FCSTD DOCUMENT  (FreeCAD 0.20R29603 (Git))
Label: CNC_Cut_Layer_Designs
License: All rights reserved
LicenseURL: http://en.wikipedia.org/wiki/All_rights_reserved
objects: Sketcher::SketchObject×10, PartDesign::Body×3
note: 13 computed .brp shape members not serialized (recipe doc carries the construction recipe); baked Part::Feature solids carry a one-line shape summary decoded from their .brp

FEATURE [Sketcher::SketchObject] Sketch007  label="Bottom"
  AttachmentOffset = pos=(496,62,0) rot=(0,0,1;0rad)
  FullyConstrained = true
  MapMode = 5
  Placement = pos=(496,62,0) rot=(0,0,1;0rad)
  Support = -> [XY_Plane004]
  sketch-geometry (20):
    g0: LineSegment StartX=-168 StartY=203 StartZ=0 EndX=168 EndY=203 EndZ=0
    g1: LineSegment StartX=168 StartY=203 StartZ=0 EndX=168 EndY=-203 EndZ=0
    g2: LineSegment StartX=168 StartY=-203 StartZ=0 EndX=-168 EndY=-203 EndZ=0
    g3: LineSegment StartX=-168 StartY=-203 StartZ=0 EndX=-168 EndY=203 EndZ=0
    g4: LineSegment StartX=-155 StartY=190 StartZ=0 EndX=155 EndY=190 EndZ=0
    g5: LineSegment StartX=155 StartY=190 StartZ=0 EndX=155 EndY=-190 EndZ=0
    g6: LineSegment StartX=155 StartY=-190 StartZ=0 EndX=-155 EndY=-190 EndZ=0
    g7: LineSegment StartX=-155 StartY=-190 StartZ=0 EndX=-155 EndY=190 EndZ=0
    g8: LineSegment StartX=155 StartY=190 StartZ=0 EndX=168 EndY=203 EndZ=0
    g9: LineSegment StartX=-168 StartY=-203 StartZ=0 EndX=-155 EndY=-190 EndZ=0
    g10: Circle CenterX=-95 CenterY=190 CenterZ=0 NormalX=0 NormalY=0 NormalZ=1 AngleXU=0 Radius=3.1
    g11: Circle CenterX=95 CenterY=190 CenterZ=0 NormalX=0 NormalY=0 NormalZ=1 AngleXU=0 Radius=3.1
    g12: Circle CenterX=155 CenterY=130 CenterZ=0 NormalX=0 NormalY=0 NormalZ=1 AngleXU=0 Radius=3.1
    g13: Circle CenterX=155 CenterY=-130 CenterZ=0 NormalX=0 NormalY=0 NormalZ=1 AngleXU=0 Radius=3.1
    g14: Circle CenterX=95 CenterY=-190 CenterZ=0 NormalX=0 NormalY=0 NormalZ=1 AngleXU=0 Radius=3.1
    g15: Circle CenterX=-95 CenterY=-190 CenterZ=0 NormalX=0 NormalY=0 NormalZ=1 AngleXU=0 Radius=3.1
    g16: Circle CenterX=-155 CenterY=-130 CenterZ=0 NormalX=0 NormalY=0 NormalZ=1 AngleXU=0 Radius=3.1
    g17: Circle CenterX=-155 CenterY=130 CenterZ=0 NormalX=0 NormalY=0 NormalZ=1 AngleXU=0 Radius=3.1
    g18: Circle CenterX=-155 CenterY=0 CenterZ=0 NormalX=0 NormalY=0 NormalZ=1 AngleXU=0 Radius=3.1
    g19: Circle CenterX=155 CenterY=0 CenterZ=0 NormalX=0 NormalY=0 NormalZ=1 AngleXU=0 Radius=3.1
  constraints (49):
    c: Coincident(g0,g1)
    c: Coincident(g1,g2)
    c: Coincident(g2,g3)
    c: Coincident(g3,g0)
    c: Horizontal(g2)
    c: Vertical(g1)
    c: DistanceX(g0,g0) = 336
    c: DistanceY(g3,g3) = 406
    c: Symmetric(g0,g0,g-2)
    c: Symmetric(g0,g2,g-1)
    c: Coincident(g4,g5)
    c: Coincident(g5,g6)
    c: Coincident(g6,g7)
    c: Coincident(g7,g4)
    c: Horizontal(g4)
    c: Horizontal(g6)
    c: Vertical(g5)
    c: Vertical(g7)
    c: Coincident(g8,g4)
    c: Coincident(g8,g0)
    c: Angle(g8) = 0.785398
    c: DistanceY(g4,g0) = 13
    c: Coincident(g9,g2)
    c: Coincident(g9,g6)
    c: Angle(g9) = 0.785398
    c: DistanceX(g2,g6) = 13
    c: PointOnObject(g10,g4)
    c: PointOnObject(g12,g5)
    c: PointOnObject(g14,g6)
    c: PointOnObject(g16,g7)
    c: Diameter(g17) = 6.2
    c: Equal(g17, g10-g13) x4
    c: Equal(g17,g16)
    c: Equal(g17,g15)
    c: Equal(g17,g14)
    c: Symmetric(g17,g16,g-1)
    c: Symmetric(g12,g13,g-1)
    c: DistanceY(g12,g17) = 0
    c: Symmetric(g15,g14,g-2)
    c: Symmetric(g10,g11,g-2)
    c: DistanceX(g10,g15) = 0
    c: DistanceX(g14,g5) = 60
    c: DistanceY(g12,g4) = 60
    c: PointOnObject(g18,g-1)
    c: PointOnObject(g19,g-1)
    c: Diameter(g19) = 6.2
    c: Equal(g19,g18)
    c: PointOnObject(g18,g7)
    c: PointOnObject(g19,g5)
FEATURE [Sketcher::SketchObject] Sketch008  label="Top"
  AttachmentOffset = pos=(496,473,0) rot=(0,0,1;0rad)
  FullyConstrained = true
  MapMode = 5
  Placement = pos=(496,473,0) rot=(0,0,1;0rad)
  Support = -> [XY_Plane004]
  sketch-geometry (18):
    g0: LineSegment StartX=-168 StartY=203 StartZ=0 EndX=168 EndY=203 EndZ=0
    g1: LineSegment StartX=168 StartY=203 StartZ=0 EndX=168 EndY=-203 EndZ=0
    g2: LineSegment StartX=168 StartY=-203 StartZ=0 EndX=-168 EndY=-203 EndZ=0
    g3: LineSegment StartX=-168 StartY=-203 StartZ=0 EndX=-168 EndY=203 EndZ=0
    g4: LineSegment StartX=-155 StartY=190 StartZ=0 EndX=155 EndY=190 EndZ=0
    g5: LineSegment StartX=155 StartY=190 StartZ=0 EndX=155 EndY=-190 EndZ=0
    g6: LineSegment StartX=155 StartY=-190 StartZ=0 EndX=-155 EndY=-190 EndZ=0
    g7: LineSegment StartX=-155 StartY=-190 StartZ=0 EndX=-155 EndY=190 EndZ=0
    g8: LineSegment StartX=155 StartY=190 StartZ=0 EndX=168 EndY=203 EndZ=0
    g9: LineSegment StartX=-168 StartY=-203 StartZ=0 EndX=-155 EndY=-190 EndZ=0
    g10: Circle CenterX=-95 CenterY=190 CenterZ=0 NormalX=0 NormalY=0 NormalZ=1 AngleXU=0 Radius=3.1
    g11: Circle CenterX=95 CenterY=190 CenterZ=0 NormalX=0 NormalY=0 NormalZ=1 AngleXU=0 Radius=3.1
    g12: Circle CenterX=155 CenterY=100 CenterZ=0 NormalX=0 NormalY=0 NormalZ=1 AngleXU=0 Radius=3.1
    g13: Circle CenterX=155 CenterY=-100 CenterZ=0 NormalX=0 NormalY=0 NormalZ=1 AngleXU=0 Radius=3.1
    g14: Circle CenterX=95 CenterY=-190 CenterZ=0 NormalX=0 NormalY=0 NormalZ=1 AngleXU=0 Radius=3.1
    g15: Circle CenterX=-95 CenterY=-190 CenterZ=0 NormalX=0 NormalY=0 NormalZ=1 AngleXU=0 Radius=3.1
    g16: Circle CenterX=-155 CenterY=-100 CenterZ=0 NormalX=0 NormalY=0 NormalZ=1 AngleXU=0 Radius=3.1
    g17: Circle CenterX=-155 CenterY=100 CenterZ=0 NormalX=0 NormalY=0 NormalZ=1 AngleXU=0 Radius=3.1
  constraints (43):
    c: Coincident(g0,g1)
    c: Coincident(g1,g2)
    c: Coincident(g2,g3)
    c: Coincident(g3,g0)
    c: Horizontal(g2)
    c: Vertical(g1)
    c: DistanceX(g0,g0) = 336
    c: DistanceY(g3,g3) = 406
    c: Symmetric(g0,g0,g-2)
    c: Symmetric(g0,g2,g-1)
    c: Coincident(g4,g5)
    c: Coincident(g5,g6)
    c: Coincident(g6,g7)
    c: Coincident(g7,g4)
    c: Horizontal(g4)
    c: Horizontal(g6)
    c: Vertical(g5)
    c: Vertical(g7)
    c: Coincident(g8,g4)
    c: Coincident(g8,g0)
    c: Angle(g8) = 0.785398
    c: DistanceY(g4,g0) = 13
    c: Coincident(g9,g2)
    c: Coincident(g9,g6)
    c: Angle(g9) = 0.785398
    c: DistanceX(g2,g6) = 13
    c: PointOnObject(g10,g4)
    c: PointOnObject(g12,g5)
    c: PointOnObject(g14,g6)
    c: PointOnObject(g16,g7)
    c: Diameter(g17) = 6.2
    c: Equal(g17, g10-g13) x4
    c: Equal(g17,g16)
    c: Equal(g17,g15)
    c: Equal(g17,g14)
    c: Symmetric(g17,g16,g-1)
    c: Symmetric(g12,g13,g-1)
    c: DistanceY(g12,g17) = 0
    c: Symmetric(g15,g14,g-2)
    c: Symmetric(g10,g11,g-2)
    c: DistanceX(g10,g15) = 0
    c: DistanceX(g14,g5) = 60
    c: DistanceY(g12,g4) = 90
FEATURE [Sketcher::SketchObject] Sketch009  label="Left"
  AttachmentOffset = pos=(60,62,0) rot=(0,0,1;1.5708rad)
  FullyConstrained = true
  MapMode = 5
  Placement = pos=(60,62,0) rot=(0,0,1;1.5708rad)
  Support = -> [XY_Plane004]
  sketch-geometry (24):
    g0: LineSegment StartX=-203 StartY=263 StartZ=0 EndX=203 EndY=263 EndZ=0
    g1: LineSegment StartX=203 StartY=263 StartZ=0 EndX=203 EndY=-263 EndZ=0
    g2: LineSegment StartX=203 StartY=-263 StartZ=0 EndX=-203 EndY=-263 EndZ=0
    g3: LineSegment StartX=-203 StartY=-263 StartZ=0 EndX=-203 EndY=263 EndZ=0
    g4: LineSegment StartX=-190 StartY=250 StartZ=0 EndX=190 EndY=250 EndZ=0
    g5: LineSegment StartX=190 StartY=250 StartZ=0 EndX=190 EndY=-250 EndZ=0
    g6: LineSegment StartX=190 StartY=-250 StartZ=0 EndX=-190 EndY=-250 EndZ=0
    g7: LineSegment StartX=-190 StartY=-250 StartZ=0 EndX=-190 EndY=250 EndZ=0
    g8: LineSegment StartX=190 StartY=250 StartZ=0 EndX=203 EndY=263 EndZ=0
    g9: LineSegment StartX=190 StartY=-250 StartZ=0 EndX=203 EndY=-263 EndZ=0
    g10: LineSegment StartX=-203 StartY=263 StartZ=0 EndX=-173 EndY=263 EndZ=0
    g11: LineSegment StartX=-173 StartY=263 StartZ=0 EndX=-173 EndY=233 EndZ=0
    g12: LineSegment StartX=-173 StartY=233 StartZ=0 EndX=-203 EndY=233 EndZ=0
    g13: LineSegment StartX=-203 StartY=233 StartZ=0 EndX=-203 EndY=263 EndZ=0
    g14: Circle CenterX=-190 CenterY=175 CenterZ=0 NormalX=0 NormalY=0 NormalZ=1 AngleXU=0 Radius=3.1
    g15: Circle CenterX=-100 CenterY=250 CenterZ=0 NormalX=0 NormalY=0 NormalZ=1 AngleXU=0 Radius=3.1
    g16: Circle CenterX=100 CenterY=250 CenterZ=0 NormalX=0 NormalY=0 NormalZ=1 AngleXU=0 Radius=3.1
    g17: Circle CenterX=190 CenterY=175 CenterZ=0 NormalX=0 NormalY=0 NormalZ=1 AngleXU=0 Radius=3.1
    g18: Circle CenterX=-190 CenterY=0 CenterZ=0 NormalX=0 NormalY=0 NormalZ=1 AngleXU=0 Radius=3.1
    g19: Circle CenterX=-190 CenterY=-175 CenterZ=0 NormalX=0 NormalY=0 NormalZ=1 AngleXU=0 Radius=3.1
    g20: Circle CenterX=-100 CenterY=-250 CenterZ=0 NormalX=0 NormalY=0 NormalZ=1 AngleXU=0 Radius=3.1
    g21: Circle CenterX=100 CenterY=-250 CenterZ=0 NormalX=0 NormalY=0 NormalZ=1 AngleXU=0 Radius=3.1
    g22: Circle CenterX=190 CenterY=-175 CenterZ=0 NormalX=0 NormalY=0 NormalZ=1 AngleXU=0 Radius=3.1
    g23: Circle CenterX=190 CenterY=0 CenterZ=0 NormalX=0 NormalY=0 NormalZ=1 AngleXU=0 Radius=3.1
  constraints (62):
    c: Coincident(g0,g1)
    c: Coincident(g1,g2)
    c: Coincident(g2,g3)
    c: Coincident(g3,g0)
    c: Horizontal(g2)
    c: Vertical(g1)
    c: Symmetric(g0,g0,g-2)
    c: Symmetric(g0,g2,g-1)
    c: DistanceX(g0,g0) = 406
    c: DistanceY(g1,g0) = 526
    c: Coincident(g4,g5)
    c: Coincident(g5,g6)
    c: Coincident(g6,g7)
    c: Coincident(g7,g4)
    c: Horizontal(g6)
    c: Vertical(g5)
    c: Vertical(g7)
    c: Coincident(g8,g4)
    c: Coincident(g8,g0)
    c: Angle(g8) = 0.785398
    c: DistanceX(g4,g0) = 13
    c: Symmetric(g4,g4,g-2)
    c: Coincident(g9,g5)
    c: Coincident(g9,g1)
    c: Angle(g9) = -0.785398
    c: Coincident(g10,g11)
    c: Coincident(g11,g12)
    c: Coincident(g12,g13)
    c: Coincident(g13,g10)
    c: Horizontal(g10)
    c: Horizontal(g12)
    c: Vertical(g11)
    c: Vertical(g13)
    c: Coincident(g10,g0)
    c: Equal(g12,g11)
    c: DistanceY(g11,g11) = 30
    c: PointOnObject(g14,g7)
    c: PointOnObject(g15,g4)
    c: PointOnObject(g17,g5)
    c: PointOnObject(g18,g-1)
    c: PointOnObject(g20,g6)
    c: PointOnObject(g23,g-1)
    c: PointOnObject(g23,g5)
    c: PointOnObject(g18,g7)
    c: Symmetric(g14,g19,g-1)
    c: Symmetric(g15,g16,g-2)
    c: Symmetric(g17,g22,g-1)
    c: DistanceY(g17,g14) = 0
    c: Symmetric(g20,g21,g-2)
    c: DistanceX(g21,g16) = 0
    c: Equal(g20,g21)
    c: Equal(g20,g22)
    c: Equal(g20,g23)
    c: Equal(g20,g17)
    c: Equal(g20,g16)
    c: Equal(g20,g15)
    c: Equal(g20,g14)
    c: Equal(g20,g18)
    c: Equal(g20,g19)
    c: Diameter(g20) = 6.2
    c: DistanceX(g16,g4) = 90
    c: DistanceY(g14,g4) = 75
FEATURE [Sketcher::SketchObject] Sketch010  label="Right"
  AttachmentOffset = pos=(60,473,0) rot=(0,0,1;1.5708rad)
  FullyConstrained = true
  MapMode = 5
  Placement = pos=(60,473,0) rot=(0,0,1;1.5708rad)
  Support = -> [XY_Plane004]
  sketch-geometry (24):
    g0: LineSegment StartX=-203 StartY=263 StartZ=0 EndX=203 EndY=263 EndZ=0
    g1: LineSegment StartX=203 StartY=263 StartZ=0 EndX=203 EndY=-263 EndZ=0
    g2: LineSegment StartX=203 StartY=-263 StartZ=0 EndX=-203 EndY=-263 EndZ=0
    g3: LineSegment StartX=-203 StartY=-263 StartZ=0 EndX=-203 EndY=263 EndZ=0
    g4: LineSegment StartX=-190 StartY=250 StartZ=0 EndX=190 EndY=250 EndZ=0
    g5: LineSegment StartX=190 StartY=250 StartZ=0 EndX=190 EndY=-250 EndZ=0
    g6: LineSegment StartX=190 StartY=-250 StartZ=0 EndX=-190 EndY=-250 EndZ=0
    g7: LineSegment StartX=-190 StartY=-250 StartZ=0 EndX=-190 EndY=250 EndZ=0
    g8: LineSegment StartX=190 StartY=250 StartZ=0 EndX=203 EndY=263 EndZ=0
    g9: LineSegment StartX=190 StartY=-250 StartZ=0 EndX=203 EndY=-263 EndZ=0
    g10: LineSegment StartX=-203 StartY=263 StartZ=0 EndX=-173 EndY=263 EndZ=0
    g11: LineSegment StartX=-173 StartY=263 StartZ=0 EndX=-173 EndY=233 EndZ=0
    g12: LineSegment StartX=-173 StartY=233 StartZ=0 EndX=-203 EndY=233 EndZ=0
    g13: LineSegment StartX=-203 StartY=233 StartZ=0 EndX=-203 EndY=263 EndZ=0
    g14: Circle CenterX=-190 CenterY=175 CenterZ=0 NormalX=0 NormalY=0 NormalZ=1 AngleXU=0 Radius=3.1
    g15: Circle CenterX=-100 CenterY=250 CenterZ=0 NormalX=0 NormalY=0 NormalZ=1 AngleXU=0 Radius=3.1
    g16: Circle CenterX=100 CenterY=250 CenterZ=0 NormalX=0 NormalY=0 NormalZ=1 AngleXU=0 Radius=3.1
    g17: Circle CenterX=190 CenterY=175 CenterZ=0 NormalX=0 NormalY=0 NormalZ=1 AngleXU=0 Radius=3.1
    g18: Circle CenterX=-190 CenterY=0 CenterZ=0 NormalX=0 NormalY=0 NormalZ=1 AngleXU=0 Radius=3.1
    g19: Circle CenterX=-190 CenterY=-175 CenterZ=0 NormalX=0 NormalY=0 NormalZ=1 AngleXU=0 Radius=3.1
    g20: Circle CenterX=-100 CenterY=-250 CenterZ=0 NormalX=0 NormalY=0 NormalZ=1 AngleXU=0 Radius=3.1
    g21: Circle CenterX=100 CenterY=-250 CenterZ=0 NormalX=0 NormalY=0 NormalZ=1 AngleXU=0 Radius=3.1
    g22: Circle CenterX=190 CenterY=-175 CenterZ=0 NormalX=0 NormalY=0 NormalZ=1 AngleXU=0 Radius=3.1
    g23: Circle CenterX=190 CenterY=0 CenterZ=0 NormalX=0 NormalY=0 NormalZ=1 AngleXU=0 Radius=3.1
  constraints (62):
    c: Coincident(g0,g1)
    c: Coincident(g1,g2)
    c: Coincident(g2,g3)
    c: Coincident(g3,g0)
    c: Horizontal(g2)
    c: Vertical(g1)
    c: Symmetric(g0,g0,g-2)
    c: Symmetric(g0,g2,g-1)
    c: DistanceX(g0,g0) = 406
    c: DistanceY(g1,g0) = 526
    c: Coincident(g4,g5)
    c: Coincident(g5,g6)
    c: Coincident(g6,g7)
    c: Coincident(g7,g4)
    c: Horizontal(g6)
    c: Vertical(g5)
    c: Vertical(g7)
    c: Coincident(g8,g4)
    c: Coincident(g8,g0)
    c: Angle(g8) = 0.785398
    c: DistanceX(g4,g0) = 13
    c: Symmetric(g4,g4,g-2)
    c: Coincident(g9,g5)
    c: Coincident(g9,g1)
    c: Angle(g9) = -0.785398
    c: Coincident(g10,g11)
    c: Coincident(g11,g12)
    c: Coincident(g12,g13)
    c: Coincident(g13,g10)
    c: Horizontal(g10)
    c: Horizontal(g12)
    c: Vertical(g11)
    c: Vertical(g13)
    c: Coincident(g10,g0)
    c: Equal(g12,g11)
    c: DistanceY(g11,g11) = 30
    c: PointOnObject(g14,g7)
    c: PointOnObject(g15,g4)
    c: PointOnObject(g17,g5)
    c: PointOnObject(g18,g-1)
    c: PointOnObject(g20,g6)
    c: PointOnObject(g23,g-1)
    c: PointOnObject(g23,g5)
    c: PointOnObject(g18,g7)
    c: Symmetric(g14,g19,g-1)
    c: Symmetric(g15,g16,g-2)
    c: Symmetric(g17,g22,g-1)
    c: DistanceY(g17,g14) = 0
    c: Symmetric(g20,g21,g-2)
    c: DistanceX(g21,g16) = 0
    c: Equal(g20,g21)
    c: Equal(g20,g22)
    c: Equal(g20,g23)
    c: Equal(g20,g17)
    c: Equal(g20,g16)
    c: Equal(g20,g15)
    c: Equal(g20,g14)
    c: Equal(g20,g18)
    c: Equal(g20,g19)
    c: Diameter(g20) = 6.2
    c: DistanceX(g16,g4) = 90
    c: DistanceY(g14,g4) = 75
FEATURE [Sketcher::SketchObject] Sketch013  label="Rear_wo_ethernet"
  AttachmentOffset = pos=(-376,122,0) rot=(0,0,1;0rad)
  FullyConstrained = false
  MapMode = 5
  Placement = pos=(-376,122,0) rot=(0,0,1;0rad)
  Support = -> [XY_Plane004]
  sketch-geometry (43):
    g0: LineSegment StartX=-168 StartY=263 StartZ=0 EndX=168 EndY=263 EndZ=0
    g1: LineSegment StartX=168 StartY=263 StartZ=0 EndX=168 EndY=-263 EndZ=0
    g2: LineSegment StartX=168 StartY=-263 StartZ=0 EndX=-168 EndY=-263 EndZ=0
    g3: LineSegment StartX=-168 StartY=-263 StartZ=0 EndX=-168 EndY=263 EndZ=0
    g4: LineSegment StartX=-155 StartY=250 StartZ=0 EndX=155 EndY=250 EndZ=0
    g5: LineSegment StartX=155 StartY=250 StartZ=0 EndX=155 EndY=-250 EndZ=0
    g6: LineSegment StartX=155 StartY=-250 StartZ=0 EndX=-155 EndY=-250 EndZ=0
    g7: LineSegment StartX=-155 StartY=-250 StartZ=0 EndX=-155 EndY=250 EndZ=0
    g8: LineSegment StartX=155 StartY=250 StartZ=0 EndX=168 EndY=263 EndZ=0
    g9: LineSegment StartX=-155 StartY=-250 StartZ=0 EndX=-168 EndY=-263 EndZ=0
    g10: Circle CenterX=-65 CenterY=250 CenterZ=0 NormalX=0 NormalY=0 NormalZ=1 AngleXU=0 Radius=3.1
    g11: Circle CenterX=65 CenterY=250 CenterZ=0 NormalX=0 NormalY=0 NormalZ=1 AngleXU=0 Radius=3.1
    g12: Circle CenterX=-155 CenterY=175 CenterZ=0 NormalX=0 NormalY=0 NormalZ=1 AngleXU=0 Radius=3.1
    g13: Circle CenterX=155 CenterY=168.039 CenterZ=0 NormalX=0 NormalY=0 NormalZ=1 AngleXU=0 Radius=3.1
    g14: Circle CenterX=-155 CenterY=0 CenterZ=0 NormalX=0 NormalY=0 NormalZ=1 AngleXU=0 Radius=3.1
    g15: Circle CenterX=155 CenterY=0 CenterZ=0 NormalX=0 NormalY=0 NormalZ=1 AngleXU=0 Radius=3.1
    g16: Circle CenterX=155 CenterY=-168.039 CenterZ=0 NormalX=0 NormalY=0 NormalZ=1 AngleXU=0 Radius=3.1
    g17: Circle CenterX=-155 CenterY=-175 CenterZ=0 NormalX=0 NormalY=0 NormalZ=1 AngleXU=0 Radius=3.1
    g18: Circle CenterX=-65 CenterY=-250 CenterZ=0 NormalX=0 NormalY=0 NormalZ=1 AngleXU=0 Radius=3.1
    g19: Circle CenterX=65 CenterY=-250 CenterZ=0 NormalX=0 NormalY=0 NormalZ=1 AngleXU=0 Radius=3.1
    g20: LineSegment StartX=-168 StartY=263 StartZ=0 EndX=-140 EndY=263 EndZ=0
    g21: LineSegment StartX=-140 StartY=263 StartZ=0 EndX=-140 EndY=235 EndZ=0
    g22: LineSegment StartX=-140 StartY=235 StartZ=0 EndX=-168 EndY=235 EndZ=0
    g23: LineSegment StartX=-168 StartY=235 StartZ=0 EndX=-168 EndY=263 EndZ=0
    g24: LineSegment StartX=-140 StartY=235 StartZ=0 EndX=-140 EndY=0 EndZ=0
    g25: LineSegment StartX=-140 StartY=235 StartZ=0 EndX=155 EndY=235 EndZ=0
    g26: LineSegment StartX=-101.201 StartY=185.045 StartZ=0 EndX=-81.2013 EndY=185.045 EndZ=0
    g27: LineSegment StartX=-77.2013 StartY=180.045 StartZ=0 EndX=-77.2013 EndY=137.045 EndZ=0
    g28: LineSegment StartX=-77.2013 StartY=137.045 StartZ=0 EndX=-105.201 EndY=137.045 EndZ=0
    g29: LineSegment StartX=-105.201 StartY=137.045 StartZ=0 EndX=-105.201 EndY=180.045 EndZ=0
    g30: LineSegment StartX=-105.201 StartY=180.045 StartZ=0 EndX=-101.201 EndY=185.045 EndZ=0
    g31: LineSegment StartX=-81.2013 StartY=185.045 StartZ=0 EndX=-77.2013 EndY=180.045 EndZ=0
    g32: LineSegment StartX=-91.2013 StartY=192.691 StartZ=0 EndX=-91.2013 EndY=126.763 EndZ=0
    g33: Circle CenterX=-111.545 CenterY=161.045 CenterZ=0 NormalX=0 NormalY=0 NormalZ=1 AngleXU=0 Radius=2
    g34: Circle CenterX=-71.5448 CenterY=161.045 CenterZ=0 NormalX=0 NormalY=0 NormalZ=1 AngleXU=0 Radius=2
    g35: LineSegment StartX=-111.545 StartY=161.045 StartZ=0 EndX=-71.5448 EndY=161.045 EndZ=0
    g36: LineSegment StartX=-47.5 StartY=208.545 StartZ=0 EndX=52.5 EndY=208.545 EndZ=0
    g37: LineSegment StartX=52.5 StartY=208.545 StartZ=0 EndX=52.5 EndY=113.545 EndZ=0
    g38: LineSegment StartX=52.5 StartY=113.545 StartZ=0 EndX=-47.5 EndY=113.545 EndZ=0
    g39: LineSegment StartX=-47.5 StartY=113.545 StartZ=0 EndX=-47.5 EndY=208.545 EndZ=0
    g40: Circle CenterX=-27.5 CenterY=161.045 CenterZ=0 NormalX=0 NormalY=0 NormalZ=1 AngleXU=0 Radius=1.6
    g41: Circle CenterX=27.5 CenterY=161.045 CenterZ=0 NormalX=0 NormalY=0 NormalZ=1 AngleXU=0 Radius=1.6
    g42: LineSegment StartX=-27.5 StartY=161.045 StartZ=0 EndX=27.5 EndY=161.045 EndZ=0
  constraints (103):
    c: Coincident(g0,g1)
    c: Coincident(g1,g2)
    c: Coincident(g2,g3)
    c: Coincident(g3,g0)
    c: Horizontal(g2)
    c: Vertical(g1)
    c: DistanceX(g0,g0) = 336
    c: DistanceY(g1,g1) = 526
    c: Symmetric(g0,g0,g-2)
    c: Symmetric(g0,g2,g-1)
    c: Coincident(g4,g5)
    c: Coincident(g5,g6)
    c: Coincident(g6,g7)
    c: Coincident(g7,g4)
    c: Horizontal(g4)
    c: Horizontal(g6)
    c: Vertical(g5)
    c: Vertical(g7)
    c: Coincident(g8,g4)
    c: Coincident(g8,g0)
    c: Coincident(g9,g6)
    c: Coincident(g9,g2)
    c: Angle(g9) = -2.35619
    c: Angle(g8) = 0.785398
    c: DistanceY(g4,g0) = 13
    c: DistanceX(g2,g6) = 13
    c: PointOnObject(g10,g4)
    c: Diameter(g12) = 6.2
    c: Equal(g12, g13-g19) x7
    c: Equal(g12,g10)
    c: Equal(g12,g11)
    c: Symmetric(g10,g11,g-2)
    c: PointOnObject(g12,g7)
    c: PointOnObject(g13,g5)
    c: PointOnObject(g15,g5)
    c: PointOnObject(g14,g7)
    c: PointOnObject(g18,g6)
    c: Symmetric(g18,g19,g-2)
    c: DistanceX(g19,g5) = 90
    c: PointOnObject(g15,g-1)
    c: Symmetric(g16,g13,g-1)
    c: PointOnObject(g14,g-1)
    c: Symmetric(g12,g17,g-1)
    c: Coincident(g20,g21)
    c: Coincident(g21,g22)
    c: Coincident(g22,g23)
    c: Coincident(g23,g20)
    c: Horizontal(g20)
    c: Horizontal(g22)
    c: Vertical(g21)
    c: Vertical(g23)
    c: Coincident(g20,g0)
    c: Equal(g22,g21)
    c: DistanceY(g21,g21) = 28
    c: Coincident(g24,g21)
    c: PointOnObject(g24,g-1)
    c: Vertical(g24)
    c: Coincident(g25,g21)
    c: PointOnObject(g25,g5)
    c: Horizontal(g25)
    c: Coincident(g27,g28)
    c: Coincident(g28,g29)
    c: Horizontal(g26)
    c: Horizontal(g28)
    c: Vertical(g27)
    c: Vertical(g29)
    c: DistanceY(g30,g31) = 0
    c: DistanceX(g30,g31) = 28
    c: DistanceY(g27,g31) = 48
    c: Coincident(g26,g30)
    c: Coincident(g29,g30)
    c: Coincident(g26,g31)
    c: Coincident(g27,g31)
    c: DistanceX(g26,g26) = 20
    c: DistanceX(g32,g27) = 14
    c: Symmetric(g26,g26,g32)
    c: DistanceY(g27,g27) = 43
    c: Coincident(g35,g33)
    c: Coincident(g35,g34)
    c: Horizontal(g35)
    c: DistanceX(g35,g35) = 40
    c: Diameter(g33) = 4
    c: Equal(g33,g34)
    c: DistanceY(g27,g34) = 24
    c: Coincident(g36,g37)
    c: Coincident(g37,g38)
    c: Coincident(g38,g39)
    c: Coincident(g39,g36)
    c: Horizontal(g36)
    c: Horizontal(g38)
    c: Vertical(g37)
    c: DistanceX(g36,g36) = 100
    c: DistanceY(g37,g37) = 95
    c: Diameter(g40) = 3.2
    c: Equal(g40,g41)
    c: Coincident(g42,g40)
    c: Coincident(g42,g41)
    c: DistanceX(g42,g42) = 55
    c: Symmetric(g36,g38,g42)
    c: DistanceX(g36,g40) = 20
    c: DistanceY(g34,g40) = 0
    c: Symmetric(g41,g40,g-2)
    c: DistanceY(g12,g4) = 75
FEATURE [Sketcher::SketchObject] Sketch022  label="Garbage"
  FullyConstrained = false
  MapMode = 5
  Support = -> [XY_Plane004]
  sketch-geometry (4):
    g0: LineSegment StartX=-543.675 StartY=391.733 StartZ=0 EndX=-207.824 EndY=391.733 EndZ=0
    g1: LineSegment StartX=-207.824 StartY=391.733 StartZ=0 EndX=-207.824 EndY=675.624 EndZ=0
    g2: LineSegment StartX=-207.824 StartY=675.624 StartZ=0 EndX=-543.675 EndY=675.624 EndZ=0
    g3: LineSegment StartX=-543.675 StartY=675.624 StartZ=0 EndX=-543.675 EndY=391.733 EndZ=0
  constraints (8):
    c: Coincident(g0,g1)
    c: Coincident(g1,g2)
    c: Coincident(g2,g3)
    c: Coincident(g3,g0)
    c: Horizontal(g0)
    c: Horizontal(g2)
    c: Vertical(g1)
    c: Vertical(g3)
FEATURE [PartDesign::Body] Body004  label="Aluminium_Layers"
  Group = -> [Sketch007,Sketch008,Sketch009,Sketch010,Sketch013,Sketch022]
  Origin = -> Origin004
FEATURE [Sketcher::SketchObject] Sketch016  label="Door"
  AttachmentOffset = pos=(-42,-8,0) rot=(0,0,1;4.71239rad)
  FullyConstrained = false
  MapMode = 5
  Placement = pos=(-42,-8,0) rot=(0,0,1;4.71239rad)
  Support = -> [XY_Plane009]
  sketch-geometry (35):
    g0: LineSegment StartX=-128.937 StartY=145 StartZ=0 EndX=130.5 EndY=145 EndZ=0
    g1: LineSegment StartX=140.5 StartY=135 StartZ=0 EndX=140.5 EndY=-135 EndZ=0
    g2: LineSegment StartX=130.5 StartY=-145 StartZ=0 EndX=-130.5 EndY=-145 EndZ=0
    g3: LineSegment StartX=-140.5 StartY=-135 StartZ=0 EndX=-140.5 EndY=-95 EndZ=0
    g4: LineSegment StartX=-127.5 StartY=125 StartZ=0 EndX=120.5 EndY=125 EndZ=0
    g5: LineSegment StartX=120.5 StartY=125 StartZ=0 EndX=120.5 EndY=-125 EndZ=0
    g6: LineSegment StartX=120.5 StartY=-125 StartZ=0 EndX=-127.5 EndY=-125 EndZ=0
    g7: LineSegment StartX=-127.5 StartY=-125 StartZ=0 EndX=-127.5 EndY=125 EndZ=0
    g8: Circle CenterX=120.5 CenterY=57.5 CenterZ=0 NormalX=0 NormalY=0 NormalZ=1 AngleXU=0 Radius=4.5
    g9: Circle CenterX=120.5 CenterY=-57.5 CenterZ=0 NormalX=0 NormalY=0 NormalZ=1 AngleXU=0 Radius=4.5
    g10: LineSegment StartX=-140.5 StartY=95 StartZ=0 EndX=-115.5 EndY=95 EndZ=0
    g11: LineSegment StartX=-115.5 StartY=95 StartZ=0 EndX=-115.5 EndY=59 EndZ=0
    g12: LineSegment StartX=-115.5 StartY=59 StartZ=0 EndX=-140.5 EndY=59 EndZ=0
    g13: LineSegment StartX=-140.5 StartY=-95 StartZ=0 EndX=-115.5 EndY=-95 EndZ=0
    g14: LineSegment StartX=-115.5 StartY=-95 StartZ=0 EndX=-115.5 EndY=-59 EndZ=0
    g15: LineSegment StartX=-115.5 StartY=-59 StartZ=0 EndX=-140.5 EndY=-59 EndZ=0
    g16: LineSegment StartX=-140.5 StartY=95 StartZ=0 EndX=-140.5 EndY=133.437 EndZ=0
    g17: LineSegment StartX=-140.5 StartY=-59 StartZ=0 EndX=-140.5 EndY=59 EndZ=0
    g18: GeomPoint X=-23.0093 Y=145 Z=0
    g19: GeomPoint X=-23.0093 Y=-145 Z=0
    g20: GeomPoint X=-140.5 Y=24.5487 Z=0
    g21: GeomPoint X=140.5 Y=24.5487 Z=0
    g22: ArcOfCircle CenterX=-128.937 CenterY=133.437 CenterZ=0 NormalX=0 NormalY=0 NormalZ=1 AngleXU=0 Radius=11.5625 StartAngle=1.5708 EndAngle=3.14159
    g23: ArcOfCircle CenterX=130.5 CenterY=135 CenterZ=0 NormalX=0 NormalY=0 NormalZ=1 AngleXU=0 Radius=10 StartAngle=9e-16 EndAngle=1.5708
    g24: ArcOfCircle CenterX=130.5 CenterY=-135 CenterZ=0 NormalX=0 NormalY=0 NormalZ=1 AngleXU=0 Radius=10 StartAngle=4.71239 EndAngle=6.28319
    g25: ArcOfCircle CenterX=-130.5 CenterY=-135 CenterZ=0 NormalX=0 NormalY=0 NormalZ=1 AngleXU=0 Radius=10 StartAngle=3.14159 EndAngle=4.71239
    g26: Circle CenterX=40.5 CenterY=125 CenterZ=0 NormalX=0 NormalY=0 NormalZ=1 AngleXU=0 Radius=3.1
    g27: Circle CenterX=-40.5 CenterY=125 CenterZ=0 NormalX=0 NormalY=0 NormalZ=1 AngleXU=0 Radius=3.1
    g28: Circle CenterX=-40.5 CenterY=-125 CenterZ=0 NormalX=0 NormalY=0 NormalZ=1 AngleXU=0 Radius=3.1
    g29: Circle CenterX=40.5 CenterY=-125 CenterZ=0 NormalX=0 NormalY=0 NormalZ=1 AngleXU=0 Radius=3.1
    g30: Circle CenterX=-127.5 CenterY=0 CenterZ=0 NormalX=0 NormalY=0 NormalZ=1 AngleXU=0 Radius=3.1
    g31: Circle CenterX=-127.5 CenterY=125 CenterZ=0 NormalX=0 NormalY=0 NormalZ=1 AngleXU=0 Radius=3.1
    g32: Circle CenterX=120.5 CenterY=125 CenterZ=0 NormalX=0 NormalY=0 NormalZ=1 AngleXU=0 Radius=3.1
    g33: Circle CenterX=-127.5 CenterY=-125 CenterZ=0 NormalX=0 NormalY=0 NormalZ=1 AngleXU=0 Radius=3.1
    g34: Circle CenterX=120.5 CenterY=-125 CenterZ=0 NormalX=0 NormalY=0 NormalZ=1 AngleXU=0 Radius=3.1
  constraints (81):
    c: Horizontal(g2)
    c: Vertical(g1)
    c: Coincident(g4,g5)
    c: Coincident(g5,g6)
    c: Coincident(g6,g7)
    c: Coincident(g7,g4)
    c: Horizontal(g4)
    c: Horizontal(g6)
    c: Vertical(g5)
    c: Vertical(g7)
    c: PointOnObject(g8,g5)
    c: DistanceY(g9,g8) = 115
    c: Symmetric(g8,g9,g-1)
    c: Diameter(g8) = 9
    c: Equal(g8,g9)
    c: Horizontal(g10)
    c: Coincident(g11,g10)
    c: Vertical(g11)
    c: Coincident(g12,g11)
    c: Horizontal(g12)
    c: DistanceX(g10,g10) = 25
    c: DistanceY(g11,g11) = 36
    c: Horizontal(g13)
    c: Coincident(g14,g13)
    c: Vertical(g14)
    c: Coincident(g15,g14)
    c: Horizontal(g15)
    c: DistanceY(g14,g14) = 36
    c: Coincident(g17,g12)
    c: Coincident(g16,g10)
    c: Tangent(g3,g16)
    c: Coincident(g3,g13)
    c: Coincident(g17,g15)
    c: Tangent(g3,g17)
    c: PointOnObject(g18,g0)
    c: PointOnObject(g19,g2)
    c: DistanceY(g19,g18) = 290
    c: PointOnObject(g20,g17)
    c: PointOnObject(g21,g1)
    c: DistanceX(g20,g21) = 281
    c: Symmetric(g21,g20,g-2)
    c: Symmetric(g11,g14,g-1)
    c: DistanceY(g10,g18) = 50
    c: Symmetric(g18,g19,g-1)
    c: Tangent(g16,g22) = 1.5708
    c: Tangent(g0,g22) = 1.5708
    c: Tangent(g1,g23) = 1.5708
    c: Tangent(g0,g23) = 1.5708
    c: Diameter(g23) = 20
    c: Horizontal(g0)
    c: Vertical(g16)
    c: Tangent(g1,g24) = 1.5708
    c: Tangent(g2,g24) = 1.5708
    c: Diameter(g24) = 20
    c: Tangent(g3,g25) = 1.5708
    c: Tangent(g2,g25) = 1.5708
    c: Diameter(g25) = 20
    c: PointOnObject(g26,g4)
    c: DistanceY(g4,g0) = 20
    c: DistanceX(g4,g1) = 20
    c: DistanceX(g10,g4) = 13
    c: DistanceY(g2,g5) = 20
    c: Symmetric(g27,g26,g-2)
    c: PointOnObject(g28,g6)
    c: DistanceX(g29,g5) = 80
    c: Symmetric(g28,g29,g-2)
    c: PointOnObject(g30,g7)
    c: PointOnObject(g30,g-1)
    c: Equal(g30,g27)
    c: Equal(g30,g26)
    c: Equal(g30,g29)
    c: Equal(g30,g28)
    c: Diameter(g30) = 6.2
    c: Coincident(g31,g4)
    c: Equal(g31,g27)
    c: Coincident(g32,g4)
    c: Equal(g32,g26)
    c: Coincident(g33,g6)
    c: Coincident(g34,g5)
    c: Equal(g34,g29)
    c: Equal(g33,g28)
FEATURE [Sketcher::SketchObject] Sketch020  label="Tray"
  AttachmentOffset = pos=(441,1.5,0) rot=(0,0,1;0rad)
  FullyConstrained = true
  MapMode = 5
  Placement = pos=(441,1.5,0) rot=(0,0,1;0rad)
  Support = -> [XY_Plane009]
  sketch-geometry (20):
    g0: LineSegment StartX=-120 StartY=150 StartZ=0 EndX=120 EndY=150 EndZ=0
    g1: LineSegment StartX=120 StartY=150 StartZ=0 EndX=120 EndY=-150 EndZ=0
    g2: LineSegment StartX=120 StartY=-150 StartZ=0 EndX=-120 EndY=-150 EndZ=0
    g3: LineSegment StartX=-120 StartY=-150 StartZ=0 EndX=-120 EndY=150 EndZ=0
    g4: LineSegment StartX=-105 StartY=135 StartZ=0 EndX=105 EndY=135 EndZ=0
    g5: LineSegment StartX=105 StartY=135 StartZ=0 EndX=105 EndY=-135 EndZ=0
    g6: LineSegment StartX=105 StartY=-135 StartZ=0 EndX=-105 EndY=-135 EndZ=0
    g7: LineSegment StartX=-105 StartY=-135 StartZ=0 EndX=-105 EndY=135 EndZ=0
    g8: LineSegment StartX=105 StartY=135 StartZ=0 EndX=120 EndY=150 EndZ=0
    g9: LineSegment StartX=-105 StartY=-135 StartZ=0 EndX=-120 EndY=-150 EndZ=0
    g10: Circle CenterX=-57.5 CenterY=135 CenterZ=0 NormalX=0 NormalY=0 NormalZ=1 AngleXU=0 Radius=3.1
    g11: Circle CenterX=-105 CenterY=0 CenterZ=0 NormalX=0 NormalY=0 NormalZ=1 AngleXU=0 Radius=3.1
    g12: Circle CenterX=57.5 CenterY=135 CenterZ=0 NormalX=0 NormalY=0 NormalZ=1 AngleXU=0 Radius=3.1
    g13: Circle CenterX=105 CenterY=0 CenterZ=0 NormalX=0 NormalY=0 NormalZ=1 AngleXU=0 Radius=3.1
    g14: Circle CenterX=-57.5 CenterY=-135 CenterZ=0 NormalX=0 NormalY=0 NormalZ=1 AngleXU=0 Radius=3.1
    g15: Circle CenterX=57.5 CenterY=-135 CenterZ=0 NormalX=0 NormalY=0 NormalZ=1 AngleXU=0 Radius=3.1
    g16: LineSegment StartX=-75 StartY=85 StartZ=0 EndX=75 EndY=85 EndZ=0
    g17: LineSegment StartX=75 StartY=85 StartZ=0 EndX=75 EndY=-85 EndZ=0
    g18: LineSegment StartX=75 StartY=-85 StartZ=0 EndX=-75 EndY=-85 EndZ=0
    g19: LineSegment StartX=-75 StartY=-85 StartZ=0 EndX=-75 EndY=85 EndZ=0
  constraints (48):
    c: Coincident(g0,g1)
    c: Coincident(g1,g2)
    c: Coincident(g2,g3)
    c: Coincident(g3,g0)
    c: Horizontal(g2)
    c: Vertical(g1)
    c: Symmetric(g0,g0,g-2)
    c: Symmetric(g0,g2,g-1)
    c: DistanceX(g0,g0) = 240
    c: DistanceY(g1,g1) = 300
    c: Coincident(g4,g5)
    c: Coincident(g5,g6)
    c: Coincident(g6,g7)
    c: Coincident(g7,g4)
    c: Horizontal(g4)
    c: Horizontal(g6)
    c: Vertical(g5)
    c: Vertical(g7)
    c: Coincident(g8,g4)
    c: Coincident(g8,g0)
    c: Coincident(g9,g6)
    c: Coincident(g9,g2)
    c: Angle(g9) = -2.35619
    c: Angle(g8) = 0.785398
    c: DistanceX(g4,g0) = 15
    c: DistanceX(g2,g6) = 15
    c: Diameter(g10) = 6.2
    c: Equal(g10, g11-g15) x5
    c: PointOnObject(g12,g4)
    c: Symmetric(g12,g10,g-2)
    c: PointOnObject(g11,g7)
    c: PointOnObject(g11,g-1)
    c: PointOnObject(g13,g5)
    c: PointOnObject(g13,g-1)
    c: PointOnObject(g15,g6)
    c: Symmetric(g14,g15,g-2)
    c: DistanceX(g10,g12) = 115
    c: DistanceX(g14,g15) = 115
    c: Coincident(g16,g17)
    c: Coincident(g17,g18)
    c: Coincident(g18,g19)
    c: Coincident(g19,g16)
    c: Horizontal(g18)
    c: Vertical(g17)
    c: Symmetric(g16,g16,g-2)
    c: Symmetric(g16,g18,g-1)
    c: DistanceX(g16,g16) = 150
    c: DistanceY(g17,g17) = 170
FEATURE [Sketcher::SketchObject] Sketch024  label="Front_Panel"
  AttachmentOffset = pos=(212,19.5,0) rot=(0,0,1;1.5708rad)
  FullyConstrained = false
  MapMode = 5
  Placement = pos=(212,19.5,0) rot=(0,0,1;1.5708rad)
  Support = -> [XY_Plane009]
  sketch-geometry (37):
    g0: LineSegment StartX=-168 StartY=105.5 StartZ=0 EndX=168 EndY=105.5 EndZ=0
    g1: LineSegment StartX=168 StartY=105.5 StartZ=0 EndX=168 EndY=-105.5 EndZ=0
    g2: LineSegment StartX=168 StartY=-105.5 StartZ=0 EndX=-168 EndY=-105.5 EndZ=0
    g3: LineSegment StartX=-168 StartY=-105.5 StartZ=0 EndX=-168 EndY=105.5 EndZ=0
    g4: LineSegment StartX=-155 StartY=92.5 StartZ=0 EndX=155 EndY=92.5 EndZ=0
    g5: LineSegment StartX=155 StartY=92.5 StartZ=0 EndX=155 EndY=-92.5 EndZ=0
    g6: LineSegment StartX=155 StartY=-92.5 StartZ=0 EndX=-155 EndY=-92.5 EndZ=0
    g7: LineSegment StartX=-155 StartY=-92.5 StartZ=0 EndX=-155 EndY=92.5 EndZ=0
    g8: Circle CenterX=-155 CenterY=50 CenterZ=0 NormalX=0 NormalY=0 NormalZ=1 AngleXU=0 Radius=3.1
    g9: Circle CenterX=-155 CenterY=-50 CenterZ=0 NormalX=0 NormalY=0 NormalZ=1 AngleXU=0 Radius=3.1
    g10: Circle CenterX=155 CenterY=50 CenterZ=0 NormalX=0 NormalY=0 NormalZ=1 AngleXU=0 Radius=3.1
    g11: Circle CenterX=155 CenterY=-50 CenterZ=0 NormalX=0 NormalY=0 NormalZ=1 AngleXU=0 Radius=3.1
    g12: Circle CenterX=80 CenterY=92.5 CenterZ=0 NormalX=0 NormalY=0 NormalZ=1 AngleXU=0 Radius=3.1
    g13: Circle CenterX=-80 CenterY=92.5 CenterZ=0 NormalX=0 NormalY=0 NormalZ=1 AngleXU=0 Radius=3.1
    g14: LineSegment StartX=-79.5 StartY=45 StartZ=0 EndX=79.5 EndY=45 EndZ=0
    g15: LineSegment StartX=79.5 StartY=45 StartZ=0 EndX=79.5 EndY=-45 EndZ=0
    g16: LineSegment StartX=79.5 StartY=-45 StartZ=0 EndX=-79.5 EndY=-45 EndZ=0
    g17: LineSegment StartX=-79.5 StartY=-45 StartZ=0 EndX=-79.5 EndY=45 EndZ=0
    g18: Circle CenterX=80.5 CenterY=53 CenterZ=0 NormalX=0 NormalY=0 NormalZ=1 AngleXU=0 Radius=1.85
    g19: Circle CenterX=-77 CenterY=53 CenterZ=0 NormalX=0 NormalY=0 NormalZ=1 AngleXU=0 Radius=1.85
    g20: Circle CenterX=-77 CenterY=-62 CenterZ=0 NormalX=0 NormalY=0 NormalZ=1 AngleXU=0 Radius=1.85
    g21: Circle CenterX=80.5 CenterY=-62 CenterZ=0 NormalX=0 NormalY=0 NormalZ=1 AngleXU=0 Radius=1.85
    g22: LineSegment StartX=95.5 StartY=-52 StartZ=0 EndX=125.2 EndY=-52 EndZ=0
    g23: LineSegment StartX=110.35 StartY=-31.0848 StartZ=0 EndX=110.35 EndY=-64.7071 EndZ=0
    g24: LineSegment StartX=103.75 StartY=-48.9 StartZ=0 EndX=116.95 EndY=-48.9 EndZ=0
    g25: LineSegment StartX=116.95 StartY=-48.9 StartZ=0 EndX=116.95 EndY=-55.1 EndZ=0
    g26: LineSegment StartX=116.95 StartY=-55.1 StartZ=0 EndX=103.75 EndY=-55.1 EndZ=0
    g27: LineSegment StartX=103.75 StartY=-55.1 StartZ=0 EndX=103.75 EndY=-48.9 EndZ=0
    g28: Circle CenterX=125.2 CenterY=-52 CenterZ=0 NormalX=0 NormalY=0 NormalZ=1 AngleXU=0 Radius=1.55
    g29: Circle CenterX=95.5 CenterY=-52 CenterZ=0 NormalX=0 NormalY=0 NormalZ=1 AngleXU=0 Radius=1.55
    g30: LineSegment StartX=95.5 StartY=-36 StartZ=0 EndX=125.2 EndY=-36 EndZ=0
    g31: LineSegment StartX=103.75 StartY=-32.9 StartZ=0 EndX=116.95 EndY=-32.9 EndZ=0
    g32: LineSegment StartX=116.95 StartY=-32.9 StartZ=0 EndX=116.95 EndY=-39.1 EndZ=0
    g33: LineSegment StartX=116.95 StartY=-39.1 StartZ=0 EndX=103.75 EndY=-39.1 EndZ=0
    g34: LineSegment StartX=103.75 StartY=-39.1 StartZ=0 EndX=103.75 EndY=-32.9 EndZ=0
    g35: Circle CenterX=125.2 CenterY=-36 CenterZ=0 NormalX=0 NormalY=0 NormalZ=1 AngleXU=0 Radius=1.55
    g36: Circle CenterX=95.5 CenterY=-36 CenterZ=0 NormalX=0 NormalY=0 NormalZ=1 AngleXU=0 Radius=1.55
  constraints (94):
    c: Coincident(g0,g1)
    c: Coincident(g1,g2)
    c: Coincident(g2,g3)
    c: Coincident(g3,g0)
    c: Horizontal(g2)
    c: Vertical(g1)
    c: Symmetric(g0,g0,g-2)
    c: Symmetric(g2,g0,g-1)
    c: DistanceX(g2,g2) = 336
    c: Coincident(g4,g5)
    c: Coincident(g5,g6)
    c: Coincident(g6,g7)
    c: Coincident(g7,g4)
    c: Horizontal(g6)
    c: Vertical(g5)
    c: Vertical(g7)
    c: DistanceX(g4,g0) = 13
    c: Symmetric(g4,g4,g-2)
    c: DistanceY(g4,g0) = 13
    c: DistanceY(g1,g5) = 13
    c: PointOnObject(g8,g7)
    c: PointOnObject(g10,g5)
    c: PointOnObject(g12,g4)
    c: Symmetric(g13,g12,g-2)
    c: Symmetric(g8,g9,g-1)
    c: Symmetric(g10,g11,g-1)
    c: Diameter(g8) = 6.2
    c: Equal(g8,g9)
    c: Equal(g8,g13)
    c: Equal(g8,g12)
    c: Equal(g8,g10)
    c: Equal(g8,g11)
    c: DistanceY(g9,g8) = 100
    c: DistanceY(g11,g10) = 100
    c: DistanceX(g13,g12) = 160
    c: Coincident(g14,g15)
    c: Coincident(g15,g16)
    c: Coincident(g16,g17)
    c: Coincident(g17,g14)
    c: Horizontal(g16)
    c: Vertical(g15)
    c: Symmetric(g14,g14,g-2)
    c: Symmetric(g14,g16,g-1)
    c: DistanceX(g14,g14) = 159
    c: DistanceY(g17,g17) = 90
    c: DistanceY(g14,g18) = 8
    c: DistanceX(g14,g18) = 1
    c: DistanceY(g14,g19) = 8
    c: DistanceX(g14,g19) = 2.5
    c: DistanceX(g15,g21) = 1
    c: DistanceY(g21,g15) = 17
    c: DistanceY(g20,g16) = 17
    c: Diameter(g19) = 3.7
    c: Equal(g19,g18)
    c: Equal(g19,g21)
    c: Equal(g19,g20)
    c: DistanceY(g2,g0) = 211
    c: Horizontal(g22)
    c: DistanceX(g22,g22) = 29.7
    c: Symmetric(g22,g22,g23)
    c: Coincident(g24,g25)
    c: Coincident(g25,g26)
    c: Coincident(g26,g27)
    c: Coincident(g27,g24)
    c: Horizontal(g26)
    c: Vertical(g27)
    c: Symmetric(g24,g24,g23)
    c: DistanceX(g24,g24) = 13.2
    c: DistanceY(g25,g25) = 6.2
    c: Coincident(g28,g22)
    c: Coincident(g29,g22)
    c: Diameter(g29) = 3.1
    c: Equal(g29,g28)
    c: Symmetric(g24,g25,g22)
    c: Horizontal(g30)
    c: Equal(g22,g30) = 29.7
    c: Coincident(g31,g32)
    c: Coincident(g32,g33)
    c: Coincident(g33,g34)
    c: Coincident(g34,g31)
    c: Horizontal(g33)
    c: Vertical(g34)
    c: Equal(g24,g31) = 13.2
    c: Equal(g25,g32) = 6.2
    c: Coincident(g35,g30)
    c: Coincident(g36,g30)
    c: Equal(g29,g36) = 3.1
    c: Equal(g36,g35)
    c: Symmetric(g31,g32,g30)
    c: DistanceX(g29,g36) = 0
    c: DistanceY(g28,g35) = 16
    c: Symmetric(g31,g31,g23)
    c: DistanceX(g21,g36) = 15
    c: DistanceY(g21,g29) = 10
FEATURE [PartDesign::Body] Body009  label="Stainless_Steel_Layers_ver3"
  Group = -> [Sketch016,Sketch020,Sketch024]
  Origin = -> Origin009
  Placement = pos=(920,0,0) rot=(0,0,1;0rad)
FEATURE [Sketcher::SketchObject] Sketch  label="Camera_LensHole"
  FullyConstrained = false
  MapMode = 5
  Support = -> [XY_Plane]
  sketch-geometry (35):
    g0: LineSegment StartX=-139 StartY=200 StartZ=0 EndX=139 EndY=200 EndZ=0
    g1: LineSegment StartX=165 StartY=174 StartZ=0 EndX=165 EndY=-174 EndZ=0
    g2: LineSegment StartX=139 StartY=-200 StartZ=0 EndX=-139 EndY=-200 EndZ=0
    g3: LineSegment StartX=-165 StartY=-174 StartZ=0 EndX=-165 EndY=174 EndZ=0
    g4: GeomPoint X=-165 Y=10.669 Z=0
    g5: GeomPoint X=165 Y=10.669 Z=0
    g6: GeomPoint X=15.8006 Y=-200 Z=0
    g7: GeomPoint X=15.8006 Y=200 Z=0
    g8: Circle CenterX=0 CenterY=0 CenterZ=0 NormalX=0 NormalY=0 NormalZ=1 AngleXU=0 Radius=19.5
    g9: LineSegment StartX=-155 StartY=190 StartZ=0 EndX=155 EndY=190 EndZ=0
    g10: LineSegment StartX=155 StartY=190 StartZ=0 EndX=155 EndY=-190 EndZ=0
    g11: LineSegment StartX=155 StartY=-190 StartZ=0 EndX=-155 EndY=-190 EndZ=0
    g12: LineSegment StartX=-155 StartY=-190 StartZ=0 EndX=-155 EndY=190 EndZ=0
    g13: LineSegment StartX=139 StartY=200 StartZ=0 EndX=139 EndY=174 EndZ=0
    g14: LineSegment StartX=139 StartY=174 StartZ=0 EndX=165 EndY=174 EndZ=0
    g15: LineSegment StartX=-139 StartY=200 StartZ=0 EndX=-139 EndY=174 EndZ=0
    g16: LineSegment StartX=-139 StartY=174 StartZ=0 EndX=-165 EndY=174 EndZ=0
    g17: LineSegment StartX=-165 StartY=-174 StartZ=0 EndX=-139 EndY=-174 EndZ=0
    g18: LineSegment StartX=-139 StartY=-174 StartZ=0 EndX=-139 EndY=-200 EndZ=0
    g19: LineSegment StartX=139 StartY=-200 StartZ=0 EndX=139 EndY=-174 EndZ=0
    g20: LineSegment StartX=139 StartY=-174 StartZ=0 EndX=165 EndY=-174 EndZ=0
    g21: Circle CenterX=-59 CenterY=190 CenterZ=0 NormalX=0 NormalY=0 NormalZ=1 AngleXU=0 Radius=2.75
    g22: Circle CenterX=59 CenterY=190 CenterZ=0 NormalX=0 NormalY=0 NormalZ=1 AngleXU=0 Radius=2.75
    g23: Circle CenterX=155 CenterY=56.6477 CenterZ=0 NormalX=0 NormalY=0 NormalZ=1 AngleXU=0 Radius=2.75
    g24: Circle CenterX=155 CenterY=-94 CenterZ=0 NormalX=0 NormalY=0 NormalZ=1 AngleXU=0 Radius=2.75
    g25: Circle CenterX=-155 CenterY=56.6477 CenterZ=0 NormalX=0 NormalY=0 NormalZ=1 AngleXU=0 Radius=2.75
    g26: Circle CenterX=-155 CenterY=-94 CenterZ=0 NormalX=0 NormalY=0 NormalZ=1 AngleXU=0 Radius=2.75
    g27: LineSegment StartX=-108 StartY=77.2878 StartZ=0 EndX=108 EndY=77.2878 EndZ=0
    g28: LineSegment StartX=108 StartY=77.2878 StartZ=0 EndX=108 EndY=-122.712 EndZ=0
    g29: LineSegment StartX=108 StartY=-122.712 StartZ=0 EndX=-108 EndY=-122.712 EndZ=0
    g30: LineSegment StartX=-108 StartY=-122.712 StartZ=0 EndX=-108 EndY=77.2878 EndZ=0
    g31: Circle CenterX=-108 CenterY=77.2878 CenterZ=0 NormalX=0 NormalY=0 NormalZ=1 AngleXU=0 Radius=1.6
    g32: Circle CenterX=108 CenterY=77.2878 CenterZ=0 NormalX=0 NormalY=0 NormalZ=1 AngleXU=0 Radius=1.6
    g33: Circle CenterX=-108 CenterY=-122.712 CenterZ=0 NormalX=0 NormalY=0 NormalZ=1 AngleXU=0 Radius=1.6
    g34: Circle CenterX=108 CenterY=-122.712 CenterZ=0 NormalX=0 NormalY=0 NormalZ=1 AngleXU=0 Radius=1.6
  constraints (87):
    c: Horizontal(g0)
    c: Horizontal(g2)
    c: Vertical(g1)
    c: Vertical(g3)
    c: PointOnObject(g4,g3)
    c: PointOnObject(g5,g1)
    c: PointOnObject(g6,g2)
    c: PointOnObject(g7,g0)
    c: Symmetric(g4,g5,g-2)
    c: Symmetric(g7,g6,g-1)
    c: Coincident(g8,g-1)
    c: Diameter(g8) = 39
    c: DistanceX(g4,g5) = 330
    c: DistanceY(g6,g7) = 400
    c: Coincident(g9,g10)
    c: Coincident(g10,g11)
    c: Coincident(g11,g12)
    c: Coincident(g12,g9)
    c: Horizontal(g9)
    c: Vertical(g12)
    c: Symmetric(g10,g11,g-2)
    c: Symmetric(g9,g10,g-1)
    c: DistanceX(g9,g5) = 10
    c: DistanceY(g9,g7) = 10
    c: Vertical(g13)
    c: Coincident(g13,g14)
    c: Horizontal(g14)
    c: Vertical(g15)
    c: Coincident(g15,g16)
    c: Horizontal(g16)
    c: Horizontal(g17)
    c: Coincident(g17,g18)
    c: Vertical(g18)
    c: Vertical(g19)
    c: Coincident(g19,g20)
    c: Horizontal(g20)
    c: Equal(g20,g19)
    c: Equal(g19,g18)
    c: Equal(g18,g17)
    c: Equal(g17,g16)
    c: Equal(g16,g15)
    c: Equal(g15,g13)
    c: Equal(g13,g14)
    c: DistanceX(g14,g14) = 26
    c: Coincident(g0,g13)
    c: Coincident(g1,g14)
    c: Coincident(g0,g15)
    c: Coincident(g3,g16)
    c: Coincident(g3,g17)
    c: Coincident(g2,g18)
    c: Coincident(g2,g19)
    c: Coincident(g1,g20)
    c: PointOnObject(g21,g9)
    c: PointOnObject(g22,g9)
    c: PointOnObject(g23,g10)
    c: PointOnObject(g24,g10)
    c: PointOnObject(g25,g12)
    c: PointOnObject(g26,g12)
    c: DistanceY(g26,g24) = 0
    c: DistanceY(g1,g24) = 80
    c: DistanceY(g25,g23) = 0
    c: DistanceX(g0,g21) = 80
    c: DistanceX(g22,g0) = 80
    c: Equal(g21,g22)
    c: Equal(g21,g23)
    c: Equal(g21,g24)
    c: Equal(g21,g26)
    c: Equal(g21,g25)
    c: Diameter(g21) = 5.5
    c: Coincident(g27,g28)
    c: Coincident(g28,g29)
    c: Coincident(g29,g30)
    c: Coincident(g30,g27)
    c: Horizontal(g29)
    c: Vertical(g30)
    c: DistanceX(g27,g27) = 216
    c: Symmetric(g27,g27,g-2)
    c: DistanceY(g28,g28) = 200
    c: Coincident(g31,g27)
    c: Coincident(g32,g27)
    c: Coincident(g33,g29)
    c: Coincident(g34,g28)
    c: Equal(g34,g32)
    c: Equal(g34,g31)
    c: Equal(g34,g33)
    c: Diameter(g34) = 3.2
    c: Vertical(g28)
FEATURE [PartDesign::Body] Body  label="Acrylic_Layers"
  Group = -> [Sketch]
  Origin = -> Origin
